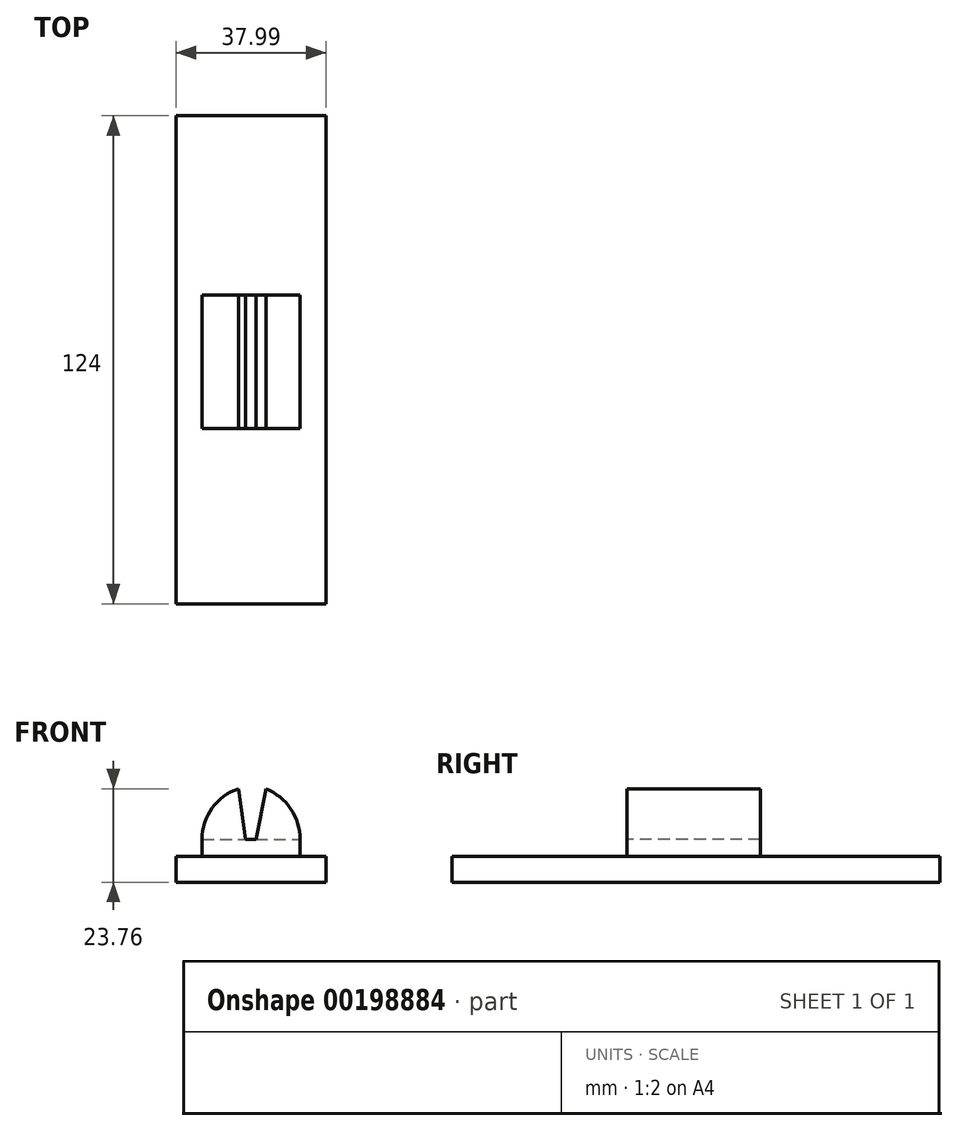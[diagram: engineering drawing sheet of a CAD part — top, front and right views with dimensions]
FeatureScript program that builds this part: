
annotation { "Feature Type Name" : "Feature", "Feature Type Description" : "" }
export const myFeature = defineFeature(function(context is Context, id is Id, definition is map)
    precondition{}
    {
        {
            var Q0;
            Q0=qCreatedBy(makeId("Top.planeOp"),FACE);
            var sketch = newSketch(context, id + "F0", { "sketchPlane" : qUnion([Q0])});
            skLineSegment(sketch, "E0.bottom", {"start": v(-19.52, 62.43) * mm, "end": v(18.47, 62.43) * mm});
            skLineSegment(sketch, "E0.top", {"start": v(-19.52, -61.57) * mm, "end": v(18.47, -61.57) * mm});
            skLineSegment(sketch, "E0.left", {"start": v(-19.52, 62.43) * mm, "end": v(-19.52, -61.57) * mm});
            skLineSegment(sketch, "E0.right", {"start": v(18.47, 62.43) * mm, "end": v(18.47, -61.57) * mm});
            skLineSegment(sketch, "E1.bottom", {"start": v(-12.97, 16.8) * mm, "end": v(11.93, 16.8) * mm});
            skLineSegment(sketch, "E1.top", {"start": v(-12.97, -17.02) * mm, "end": v(11.93, -17.02) * mm});
            skLineSegment(sketch, "E1.left", {"start": v(-12.97, 16.8) * mm, "end": v(-12.97, -17.02) * mm});
            skLineSegment(sketch, "E1.right", {"start": v(11.93, 16.8) * mm, "end": v(11.93, -17.02) * mm});
            skSolve(sketch);
        }
        {
            var Q0;
            Q0=makeQuery(id+"F0.imprint","IMPRINT",FACE,{"disambiguationData":[TD([[makeQuery(id+"F0.imprint","IMPRINT",EDGE,{"derivedFrom":sQuery(id+"F0.wireOp",EDGE,"E0.bottom")}),-1.0]])]});
            extrude(context, id + "F1", {"entities" : qUnion([Q0]), "depth" : 6.6 * mm});
        }
        {
            var Q0;
            Q0=makeQuery(id+"F0.imprint","IMPRINT",FACE,{"disambiguationData":[TD([[makeQuery(id+"F0.imprint","IMPRINT",EDGE,{"derivedFrom":sQuery(id+"F0.wireOp",EDGE,"E1.bottom")}),-1.0]])]});
            extrude(context, id + "F2", {"entities" : qUnion([Q0]), "operationType" : NewBodyOperationType.ADD, "depth" : 10.9 * mm});
        }
        {
            var Q0;
            Q0=makeQuery(id+"F2.opExtrude","SWEPT_FACE",FACE,{"disambiguationData":[OSD([sQuery(id+"F0.wireOp",EDGE,"E1.top")])]});
            var sketch = newSketch(context, id + "F3", { "sketchPlane" : qUnion([Q0])});
            skArc(sketch, "E2", {"start": v(-3.74, 23.76) * mm, "mid": v(-10.43, 18.82) * mm, "end": v(-12.97, 10.9) * mm});
            skArc(sketch, "E3", {"start": v(11.93, 10.9) * mm, "mid": v(9.56, 18.63) * mm, "end": v(3.27, 23.71) * mm});
            skLineSegment(sketch, "E4", {"start": v(-3.74, 23.76) * mm, "end": v(-1.88, 10.9) * mm});
            skLineSegment(sketch, "E5", {"start": v(3.27, 23.71) * mm, "end": v(0.6, 10.5) * mm});
            skSolve(sketch);
        }
        {
            var Q0;
            {var subQ0=sQuery(id+"F3.wireOp",EDGE,"E3");Q0=makeQuery(id+"F3.imprint","IMPRINT",FACE,{"disambiguationData":[TD([[makeQuery(id+"F3.imprint","IMPRINT",EDGE,{"derivedFrom":subQ0}),1.0]])]});}
            var Q1;
            {var subQ0=sQuery(id+"F3.wireOp",EDGE,"E2");Q1=makeQuery(id+"F3.imprint","IMPRINT",FACE,{"disambiguationData":[TD([[makeQuery(id+"F3.imprint","IMPRINT",EDGE,{"derivedFrom":subQ0}),1.0]])]});}
            extrude(context, id + "F4", {"entities" : qUnion([Q0, Q1]), "operationType" : NewBodyOperationType.ADD, "oppositeDirection" : true, "depth" : 33.9 * mm});
        }
    });
